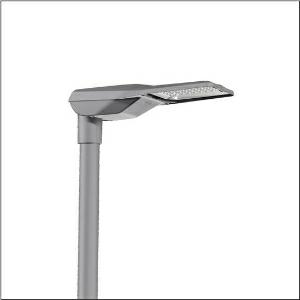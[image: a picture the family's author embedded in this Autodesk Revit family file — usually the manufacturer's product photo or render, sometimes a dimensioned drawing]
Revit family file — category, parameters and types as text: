
# Revit family: streetlight_sl_21_iq_mini___p1_0a_5xe2a31g08gb_9f18
name_source: partatom
category: Lighting Fixtures
units: mm (PartAtom-declared; Revit-internal decimal feet)

## family parameters
Cut with Voids When Loaded = No
Host = Face
Light Source = No
Part Type = Normal
Room Calculation Point = No
Round Connector Dimension = Use Diameter
Shared = No

## types (1)
- --- (1 x LED, 5680 lm, 37.1 W, 3000K)
    Apparent Load = 37 VA
    CIE Flux Codes = 21 50 90 100 100
    Color Rendering = 70
    Color Temperature = 3000K
    Default Elevation = 1800 mm
    Description = Streetlight SL 21 iQ mini, mast luminaire, primary light control with lens, of PMMA, primary optical cover: cover, of toughened safety glass, transparent, light distribution: P1.0a, light emission: direct distribution, primary light characteristic: asymmetric, installation type: post-top, side-entry, LED, High Power LED, rated luminous flux: 5.680lm, luminous efficacy: 153lm/W, light colour: 730, colour temperature: 3000K, control gear: iQ Street-Remote, control: Street-Remote, Auto-Match, Temp-Guard, Lumen-Switch, Night-Set, Smart-Wire, Light-Fading, Desk-Remote (wireless, voltage-free reading and setting of iQ features in the workshop via application-optimized NFC function/RFID function), optimised constant luminous flux control (CLO 2.0), pre-setting: linear dimming characteristic, mains connection: 220..240V, AC, 50/60Hz, start of lifetime: 37W, end of service life: 39W, reduction: 18W, luminaire housing, of diecast aluminium, powder-coated, Siteco® metallic grey (DB 702S), corrosivity category C5 mid according to DIN EN ISO 12944, please order mast flange separately, inclination adjustable: 0°, 5°, 10°, 15°, sealing non-destructively replaceable, multi-level sealing system, length: 628mm, width: 235mm, height: 110mm, mast flange for spigot size: 42mm (side-entry): 5XC10008XM4, 60/48mm (side-entry/post-top): 5XC10108XM2, 76/60mm (side-entry/post-top): 5XC10108XM1, mounting height: 4..8m, protection rating (complete): IP66, insulation class (complete): insulation class II (safety insulation), certification: CE, ENEC, ENEC+, VDE, impact resistance: IK10, permissible operating ambient temperature for outdoor applications: -40..+50°C, standard-compliant lighting for roads and squares, packaging unit: 1 piece

Light Distribution: P1.0a
    Height = 110 mm
    Lamp = 1 x LED
    Lamp Light Flux = 5680 lm
    Lamp Power = 37.1 W
    Lamp count = 1
    Length = 625 mm
    Luminous efficacy = 153 lm/W
    Manufacturer = Siteco
    ModVariant = No
    Model = 5XE2A31G08GB
    Number of Poles = 1
    OnlyDefault = Yes
    Power Factor = 1
    Product Name = Streetlight SL 21 iQ mini | P1.0a
    Product group = mast luminaire | pylon top
    ProductGroupID = 6100
    Protection Class = Protection class II
    Protection Degree = IP 66
    RLX_Detail_Level = 1
    RLX_Emergency_Light_Flux = 0 lm
    RLX_Emergency_Type = 0
    RLX_Emergency_Type_DB = No
    RlxData = <blob elided: 37545 chars, md5=bd62bacb>
    Socket = socket
    Standby Power = 0 W
    System Light Flux = 5680 lm
    System Power = 37 W
    Type Comments = factory setting: luminous flux: 100 % | dim-lin: 254 | 385 mA
    Type Image = l_1003519.jpg
    URL = http://relux.com
    VarID = @adj_208115
    Voltage = 0 V
    Weight = 0.00 kg
    Width = 234 mm

## geometry (parser evidence)
native form markers: Blend x4, Sweep x10
no freeform markers — native parametric forms only
